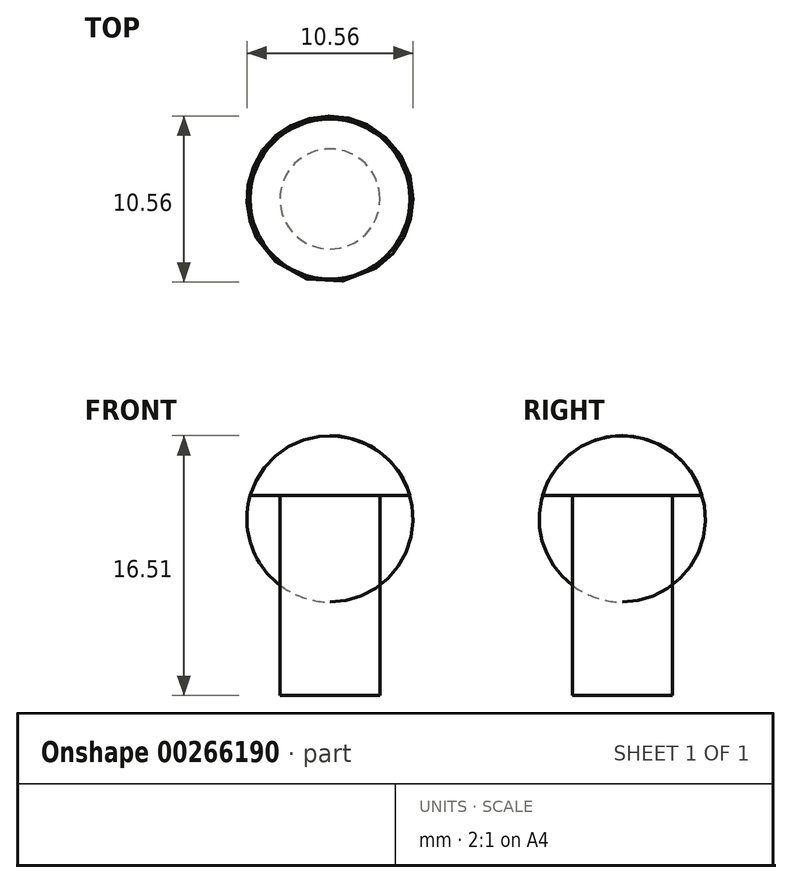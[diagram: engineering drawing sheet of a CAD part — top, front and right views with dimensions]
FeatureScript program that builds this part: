
annotation { "Feature Type Name" : "Feature", "Feature Type Description" : "" }
export const myFeature = defineFeature(function(context is Context, id is Id, definition is map)
    precondition{}
    {
        {
            var Q0;
            Q0=qCreatedBy(makeId("Front.planeOp"),FACE);
            var sketch = newSketch(context, id + "F0", { "sketchPlane" : qUnion([Q0])});
            skLineSegment(sketch, "E0", {"start": v(0, 0) * mm, "end": v(0, 16.51) * mm});
            skLineSegment(sketch, "E1", {"start": v(0, 0) * mm, "end": v(3.17, 0) * mm});
            skLineSegment(sketch, "E2", {"start": v(3.17, 0) * mm, "end": v(3.17, 12.7) * mm});
            skLineSegment(sketch, "E3", {"start": v(3.17, 12.7) * mm, "end": v(5.08, 12.7) * mm});
            skArc(sketch, "E4", {"start": v(5.08, 12.7) * mm, "mid": v(3.18, 15.45) * mm, "end": v(0, 16.51) * mm});
            skSolve(sketch);
        }
        {
            var Q0;
            Q0=makeQuery(id+"F0.imprint","IMPRINT",FACE,{"disambiguationData":[TD([[makeQuery(id+"F0.imprint","IMPRINT",EDGE,{"derivedFrom":sQuery(id+"F0.wireOp",EDGE,"E0")}),-1.0]])]});
            var Q1;
            Q1=sQuery(id+"F0.wireOp",EDGE,"E0");
            revolve(context, id + "F1", {"entities" : qUnion([Q0]), "axis" : qUnion([Q1]), "revolveType" : RevolveType.FULL});
        }
    });
